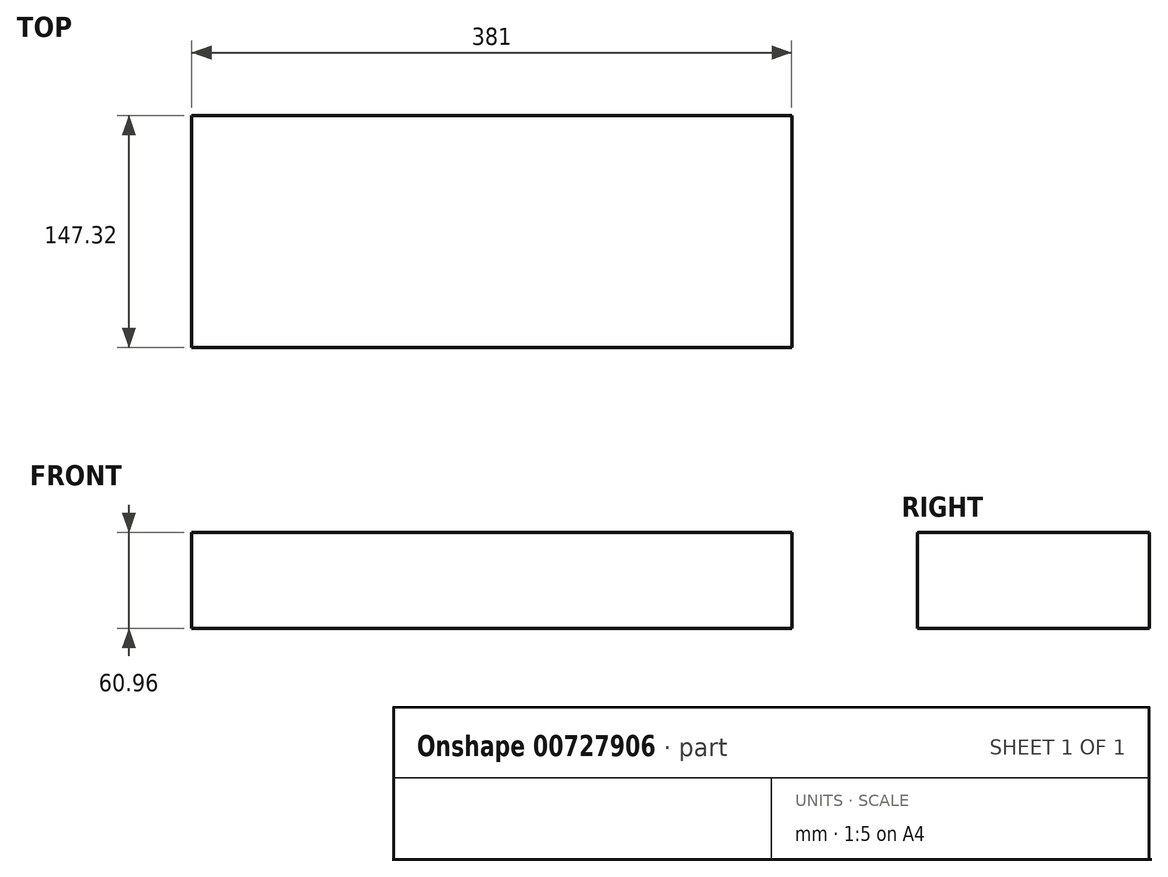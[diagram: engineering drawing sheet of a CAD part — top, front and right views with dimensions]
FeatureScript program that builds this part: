
annotation { "Feature Type Name" : "Feature", "Feature Type Description" : "" }
export const myFeature = defineFeature(function(context is Context, id is Id, definition is map)
    precondition{}
    {
        {
            var Q0;
            Q0=qCreatedBy(makeId("Front.planeOp"),FACE);
            var sketch = newSketch(context, id + "F0", { "sketchPlane" : qUnion([Q0])});
            skLineSegment(sketch, "E0.bottom", {"start": v(-306.94, 62.32) * mm, "end": v(74.06, 62.32) * mm});
            skLineSegment(sketch, "E0.top", {"start": v(-306.94, 1.36) * mm, "end": v(74.06, 1.36) * mm});
            skLineSegment(sketch, "E0.left", {"start": v(-306.94, 62.32) * mm, "end": v(-306.94, 1.36) * mm});
            skLineSegment(sketch, "E0.right", {"start": v(74.06, 62.32) * mm, "end": v(74.06, 1.36) * mm});
            skLineSegment(sketch, "E1.bottom", {"start": v(-212.96, 128.36) * mm, "end": v(-19.92, 128.36) * mm});
            skLineSegment(sketch, "E1.top", {"start": v(-212.96, 62.32) * mm, "end": v(-19.92, 62.32) * mm});
            skLineSegment(sketch, "E1.left", {"start": v(-212.96, 128.36) * mm, "end": v(-212.96, 62.32) * mm});
            skLineSegment(sketch, "E1.right", {"start": v(-19.92, 128.36) * mm, "end": v(-19.92, 62.32) * mm});
            skArc(sketch, "E2", {"start": v(-181.2, 128.36) * mm, "mid": v(-116.44, 75.2) * mm, "end": v(-51.67, 128.36) * mm});
            skSolve(sketch);
        }
        {
            var Q0;
            Q0=makeQuery(id+"F0.imprint","IMPRINT",FACE,{"disambiguationData":[TD([[makeQuery(id+"F0.imprint","IMPRINT",EDGE,{"derivedFrom":sQuery(id+"F0.wireOp",EDGE,"E0.top")}),1.0]])]});
            var Q1;
            Q1=makeQuery(id+"F0.imprint","IMPRINT",FACE,{"disambiguationData":[TD([[makeQuery(id+"F0.imprint","IMPRINT",EDGE,{"derivedFrom":sQuery(id+"F0.wireOp",EDGE,"E1.top")}),1.0]])]});
            extrude(context, id + "F1", {"entities" : qUnion([Q0, Q1]), "depth" : 147.32 * mm, "offsetDistance" : 25.4 * mm});
        }
    });
